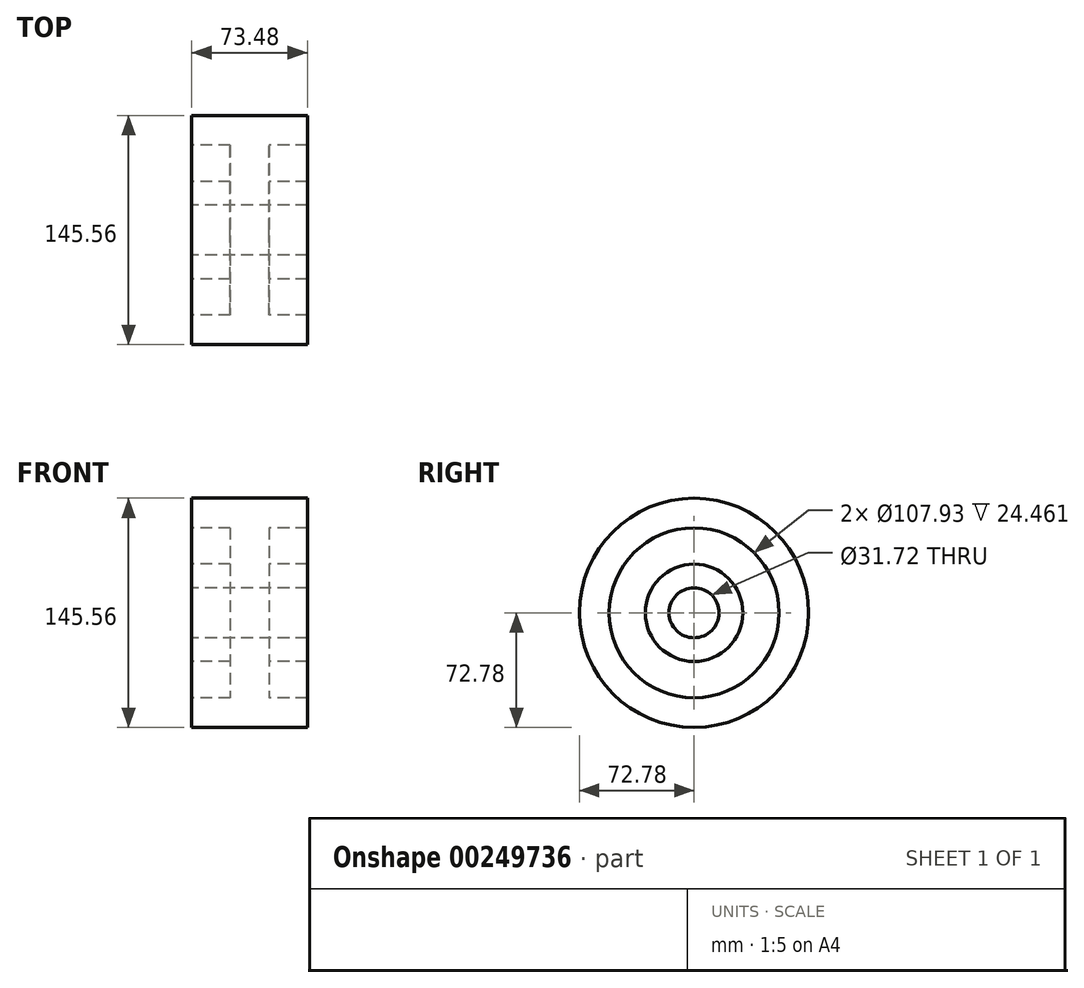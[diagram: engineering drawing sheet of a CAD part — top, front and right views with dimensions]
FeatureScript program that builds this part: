
annotation { "Feature Type Name" : "Feature", "Feature Type Description" : "" }
export const myFeature = defineFeature(function(context is Context, id is Id, definition is map)
    precondition{}
    {
        {
            var Q0;
            Q0=qCreatedBy(makeId("Front.planeOp"),FACE);
            var sketch = newSketch(context, id + "F0", { "sketchPlane" : qUnion([Q0])});
            skLineSegment(sketch, "E0", {"start": v(0, 88.3) * mm, "end": v(0, -88.1) * mm, "construction": true});
            skLineSegment(sketch, "E1", {"start": v(-113.8, 0) * mm, "end": v(110.59, 0) * mm, "construction": true});
            skLineSegment(sketch, "E2", {"start": v(0, 15.86) * mm, "end": v(36.74, 15.86) * mm});
            skLineSegment(sketch, "E3", {"start": v(36.74, 15.86) * mm, "end": v(36.74, 30.91) * mm});
            skLineSegment(sketch, "E4", {"start": v(36.74, 30.91) * mm, "end": v(12.28, 30.91) * mm});
            skLineSegment(sketch, "E5", {"start": v(12.28, 30.91) * mm, "end": v(12.28, 53.96) * mm});
            skLineSegment(sketch, "E6", {"start": v(12.28, 53.96) * mm, "end": v(36.74, 53.96) * mm});
            skLineSegment(sketch, "E7", {"start": v(36.74, 53.96) * mm, "end": v(36.74, 72.78) * mm});
            skLineSegment(sketch, "E8", {"start": v(36.74, 72.78) * mm, "end": v(0, 72.78) * mm});
            skLineSegment(sketch, "E9.MirrorCS", {"start": v(0, 15.86) * mm, "end": v(-36.74, 15.86) * mm});
            skLineSegment(sketch, "E10.MirrorCS", {"start": v(-36.74, 15.86) * mm, "end": v(-36.74, 30.91) * mm});
            skLineSegment(sketch, "E11.MirrorCS", {"start": v(-36.74, 30.91) * mm, "end": v(-12.28, 30.91) * mm});
            skLineSegment(sketch, "E12.MirrorCS", {"start": v(-12.28, 30.91) * mm, "end": v(-12.28, 53.96) * mm});
            skLineSegment(sketch, "E13.MirrorCS", {"start": v(-12.28, 53.96) * mm, "end": v(-36.74, 53.96) * mm});
            skLineSegment(sketch, "E14.MirrorCS", {"start": v(-36.74, 72.78) * mm, "end": v(0, 72.78) * mm});
            skLineSegment(sketch, "E15.MirrorCS", {"start": v(-36.74, 53.96) * mm, "end": v(-36.74, 72.78) * mm});
            skSolve(sketch);
        }
        {
            var Q0;
            Q0 = qSketchRegion(id + "F0", true);
            var Q1;
            Q1=sQuery(id+"F0.wireOp",EDGE,"E1");
            revolve(context, id + "F1", {"entities" : qUnion([Q0]), "axis" : qUnion([Q1]), "revolveType" : RevolveType.FULL});
        }
    });
